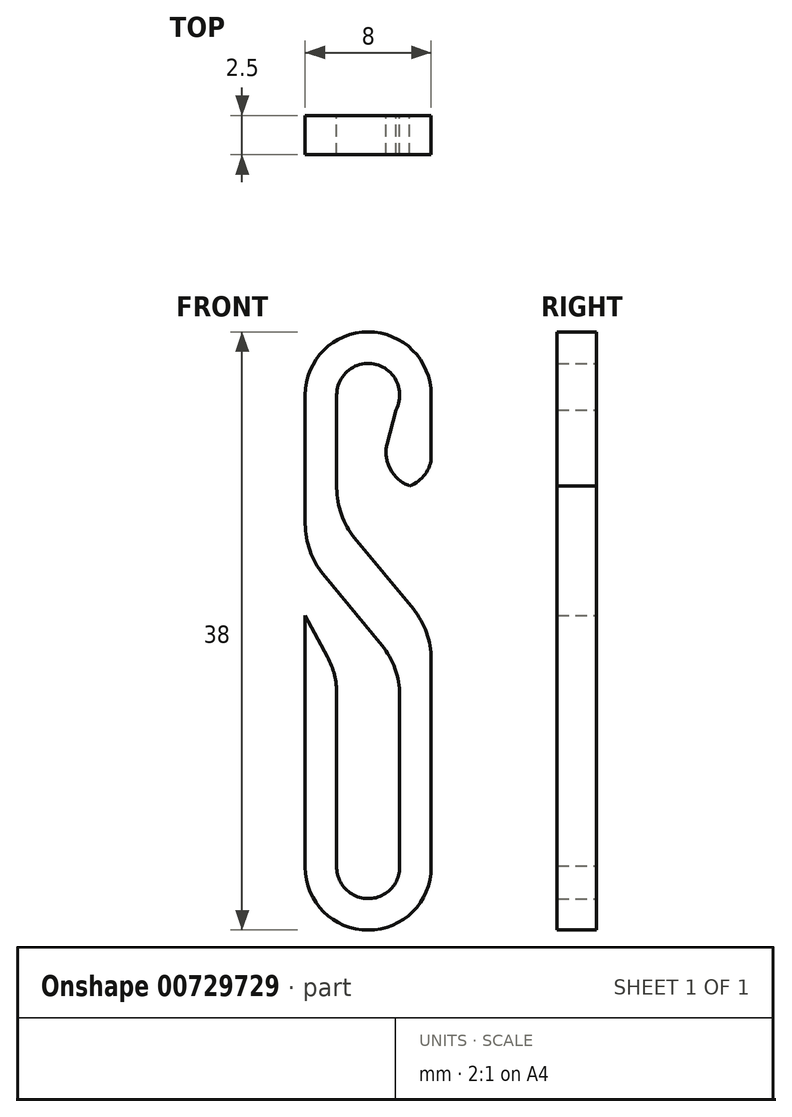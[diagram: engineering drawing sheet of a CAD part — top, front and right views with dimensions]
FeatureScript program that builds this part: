
annotation { "Feature Type Name" : "Feature", "Feature Type Description" : "" }
export const myFeature = defineFeature(function(context is Context, id is Id, definition is map)
    precondition{}
    {
        {
            var Q0;
            Q0=qCreatedBy(makeId("Front.planeOp"),FACE);
            var sketch = newSketch(context, id + "F0", { "sketchPlane" : qUnion([Q0])});
            skArc(sketch, "E0", {"start": v(1.75, -0.97) * mm, "mid": v(0.5, 1.94) * mm, "end": v(-2, 0) * mm});
            skArc(sketch, "E1", {"start": v(-2, -29.93) * mm, "mid": v(-0.03, -32) * mm, "end": v(2, -30) * mm});
            skArc(sketch, "E2", {"start": v(4, 0) * mm, "mid": v(0, 4) * mm, "end": v(-4, 0) * mm});
            skArc(sketch, "E3", {"start": v(-4, -30) * mm, "mid": v(0, -34) * mm, "end": v(4, -30) * mm});
            skLineSegment(sketch, "E4", {"start": v(-4, 0) * mm, "end": v(-4, -10) * mm});
            skLineSegment(sketch, "E5", {"start": v(-4, -10) * mm, "end": v(2, -17.3) * mm});
            skLineSegment(sketch, "E6", {"start": v(2, -17.3) * mm, "end": v(2, -30) * mm});
            skLineSegment(sketch, "E7", {"start": v(-2, 0) * mm, "end": v(-2, -7.7) * mm});
            skLineSegment(sketch, "E8", {"start": v(-2, -7.7) * mm, "end": v(4, -15) * mm});
            skLineSegment(sketch, "E9", {"start": v(4, -15) * mm, "end": v(4, -30) * mm});
            skLineSegment(sketch, "E10", {"start": v(1.75, -0.97) * mm, "end": v(1, -3.87) * mm});
            skLineSegment(sketch, "E11", {"start": v(1, -3.87) * mm, "end": v(2, -5.87) * mm});
            skLineSegment(sketch, "E12", {"start": v(2, -5.87) * mm, "end": v(4, -5.87) * mm});
            skLineSegment(sketch, "E13", {"start": v(4, -5.87) * mm, "end": v(4, 0) * mm});
            skLineSegment(sketch, "E14", {"start": v(-2, -29.93) * mm, "end": v(-2, -17.75) * mm});
            skLineSegment(sketch, "E15", {"start": v(-2, -17.75) * mm, "end": v(-4, -14) * mm});
            skLineSegment(sketch, "E16", {"start": v(-4, -14) * mm, "end": v(-4, -30) * mm});
            skPoint(sketch, "E17.orphan", {"position": v(2, 0) * mm});
            skSolve(sketch);
        }
        {
            var Q0;
            Q0=makeQuery(id+"F0.imprint","IMPRINT",FACE,{"disambiguationData":[TD([[makeQuery(id+"F0.imprint","IMPRINT",EDGE,{"derivedFrom":sQuery(id+"F0.wireOp",EDGE,"E0")}),-1.0]])]});
            extrude(context, id + "F1", {"entities" : qUnion([Q0]), "depth" : 2.5 * mm, "offsetDistance" : 25 * mm});
        }
        {
            var Q0;
            Q0=makeQuery(id+"F1.opExtrude","SWEPT_EDGE",EDGE,{"disambiguationData":[OSD([sQuery(id+"F0.wireOp",EDGE,"E4"),sQuery(id+"F0.wireOp",EDGE,"E5")])]});
            var Q1;
            Q1=makeQuery(id+"F1.opExtrude","SWEPT_EDGE",EDGE,{"disambiguationData":[OSD([sQuery(id+"F0.wireOp",EDGE,"E5"),sQuery(id+"F0.wireOp",EDGE,"E6")])]});
            var Q2;
            Q2=makeQuery(id+"F1.opExtrude","SWEPT_EDGE",EDGE,{"disambiguationData":[OSD([sQuery(id+"F0.wireOp",EDGE,"E8"),sQuery(id+"F0.wireOp",EDGE,"E9")])]});
            var Q3;
            Q3=makeQuery(id+"F1.opExtrude","SWEPT_EDGE",EDGE,{"disambiguationData":[OSD([sQuery(id+"F0.wireOp",EDGE,"E7"),sQuery(id+"F0.wireOp",EDGE,"E8")])]});
            var Q4;
            Q4=makeQuery(id+"F1.opExtrude","SWEPT_EDGE",EDGE,{"disambiguationData":[OSD([sQuery(id+"F0.wireOp",EDGE,"E14"),sQuery(id+"F0.wireOp",EDGE,"E15")])]});
            fillet(context, id + "F2", {"entities" : qUnion([Q0, Q1, Q2, Q3, Q4]), "radius" : 5 * mm, "tangentPropagation" : true, "allowEdgeOverflow" : false});
        }
        {
            var Q0;
            Q0=makeQuery(id+"F1.opExtrude","SWEPT_EDGE",EDGE,{"disambiguationData":[OSD([sQuery(id+"F0.wireOp",EDGE,"E10"),sQuery(id+"F0.wireOp",EDGE,"E11")])]});
            var Q1;
            Q1=makeQuery(id+"F1.opExtrude","SWEPT_EDGE",EDGE,{"disambiguationData":[OSD([sQuery(id+"F0.wireOp",EDGE,"E11"),sQuery(id+"F0.wireOp",EDGE,"E12")])]});
            var Q2;
            Q2=makeQuery(id+"F1.opExtrude","SWEPT_EDGE",EDGE,{"disambiguationData":[OSD([sQuery(id+"F0.wireOp",EDGE,"E12"),sQuery(id+"F0.wireOp",EDGE,"E13")])]});
            fillet(context, id + "F3", {"entities" : qUnion([Q0, Q1, Q2]), "radius" : 2 * mm, "tangentPropagation" : true, "allowEdgeOverflow" : false});
        }
    });
